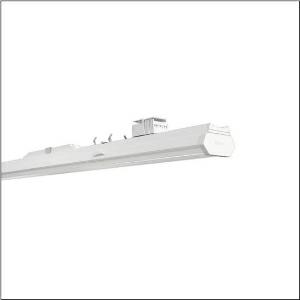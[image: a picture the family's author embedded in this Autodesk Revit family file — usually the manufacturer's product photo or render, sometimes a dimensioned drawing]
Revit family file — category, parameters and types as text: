
# Revit family: licross_r__11_protected_extreme_mo_51tp12dn49xfe_db7b
name_source: partatom
category: Lighting Fixtures
units: mm (PartAtom-declared; Revit-internal decimal feet)

## family parameters
Cut with Voids When Loaded = No
Host = Face
Light Source = No
Part Type = Normal
Room Calculation Point = No
Round Connector Dimension = Use Diameter
Shared = No

## types (1)
- --- (1 x LED, 9020 lm, 56.2 W, 4000K)
    Apparent Load = 56 VA
    CIE Flux Codes = 73 92 98 99 100
    Color Rendering = 80
    Color Temperature = 4000K
    Default Elevation = 1800 mm
    Description = Licross® 11 Protected extreme MOluminaire insert, length: 1.500mm, width: 90mm, height: 101mm, LED rated luminous flux: 9.020lm, light colour: 840, control gear: DALI 2, control gear: ECG DALI, with plug, 5-pole, with phase selection, mains connection: 220..240V, AC, 50/60Hz, halogen-free wiring, primary optical cover: cover, of PMMA, light emission: direct with ceiling illumination distribution, protection rating (complete): IP64, insulation class (complete): insulation class I (protective earthing), certification: CE, ENEC, VDE, protection symbol: D if used in an environment with conductive dust loads with corresponding accessories, permissible ambient temperature for indoor applications: -25..+50°C, reducing of maximum allowable ambient temperature of 5°C with ceiling mounting, corresponds to IFS (International Featured Standards) requirements for safety and quality in the food industry, packaging unit: 1 piece
    Height = 92 mm
    Lamp = 1 x LED
    Lamp Light Flux = 9020 lm
    Lamp Power = 56.2 W
    Lamp count = 1
    Length = 1500 mm
    Luminous efficacy = 161 lm/W
    Manufacturer = Siteco
    ModVariant = No
    Model = 51TP12DN49XFE
    Mounting Place = Ceiling
    Mounting Type = Pendant
    Number of Poles = 1
    OnlyDefault = Yes
    Power Factor = 1
    Product Name = Licross® 11 Protected extreme MO
    Product group = luminaire insert
    ProductGroupID = 902
    Protection Class = Protection class I
    Protection Degree = IP 64
    RLX_Detail_Level = 1
    RlxData = <blob elided: 23957 chars, md5=c7eebc42>
    Socket = socket
    Standby Power = 0 W
    System Light Flux = 9020 lm
    System Power = 56 W
    Type Comments = factory setting: luminous flux: 100 % | dim-lin: 254 | 370 mA
    Type Image = l_1256148.jpg
    URL = http://relux.com
    VarID = @adj_132754
    Voltage = 0 V
    Weight = 0.00 kg
    Width = 88 mm

## geometry (parser evidence)
native form markers: Blend x4, Sweep x9
no freeform markers — native parametric forms only
